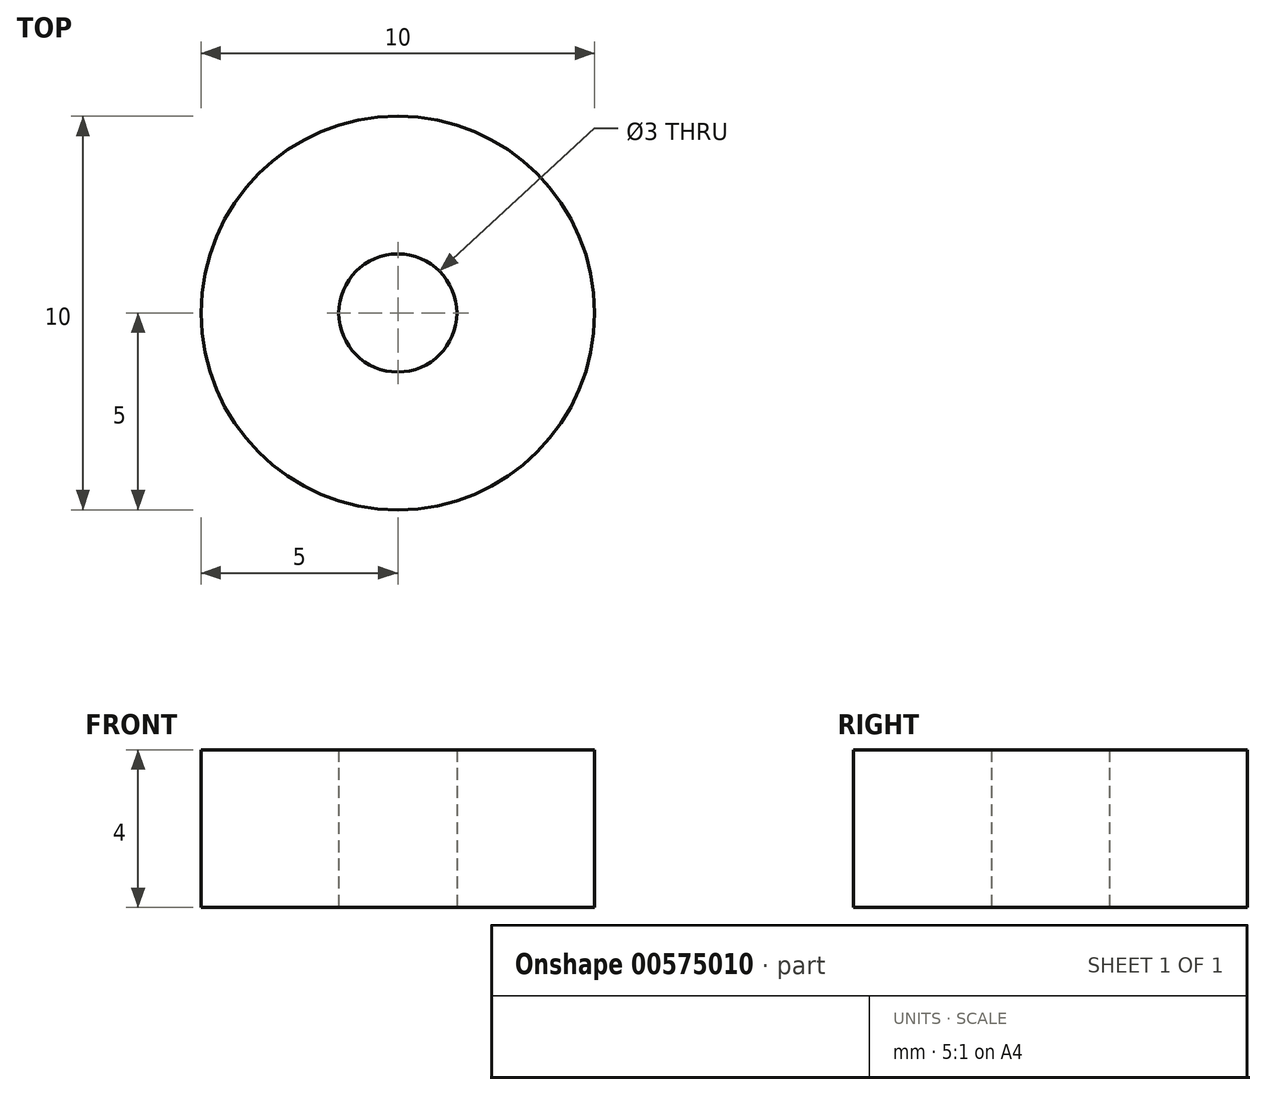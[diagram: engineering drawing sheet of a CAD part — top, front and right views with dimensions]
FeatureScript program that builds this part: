
annotation { "Feature Type Name" : "Feature", "Feature Type Description" : "" }
export const myFeature = defineFeature(function(context is Context, id is Id, definition is map)
    precondition{}
    {
        {
            var Q0;
            Q0=qCreatedBy(makeId("Top.planeOp"),FACE);
            var sketch = newSketch(context, id + "F0", { "sketchPlane" : qUnion([Q0])});
            skCircle(sketch, "E0", {"center": v(0, 0) * mm, "radius": 5 * mm});
            skCircle(sketch, "E1", {"center": v(0, 0) * mm, "radius": 1.5 * mm});
            skSolve(sketch);
        }
        {
            var Q0;
            Q0 = qSketchRegion(id + "F0", true);
            extrude(context, id + "F1", {"entities" : qUnion([Q0]), "depth" : 4 * mm, "offsetDistance" : 25 * mm});
        }
    });
